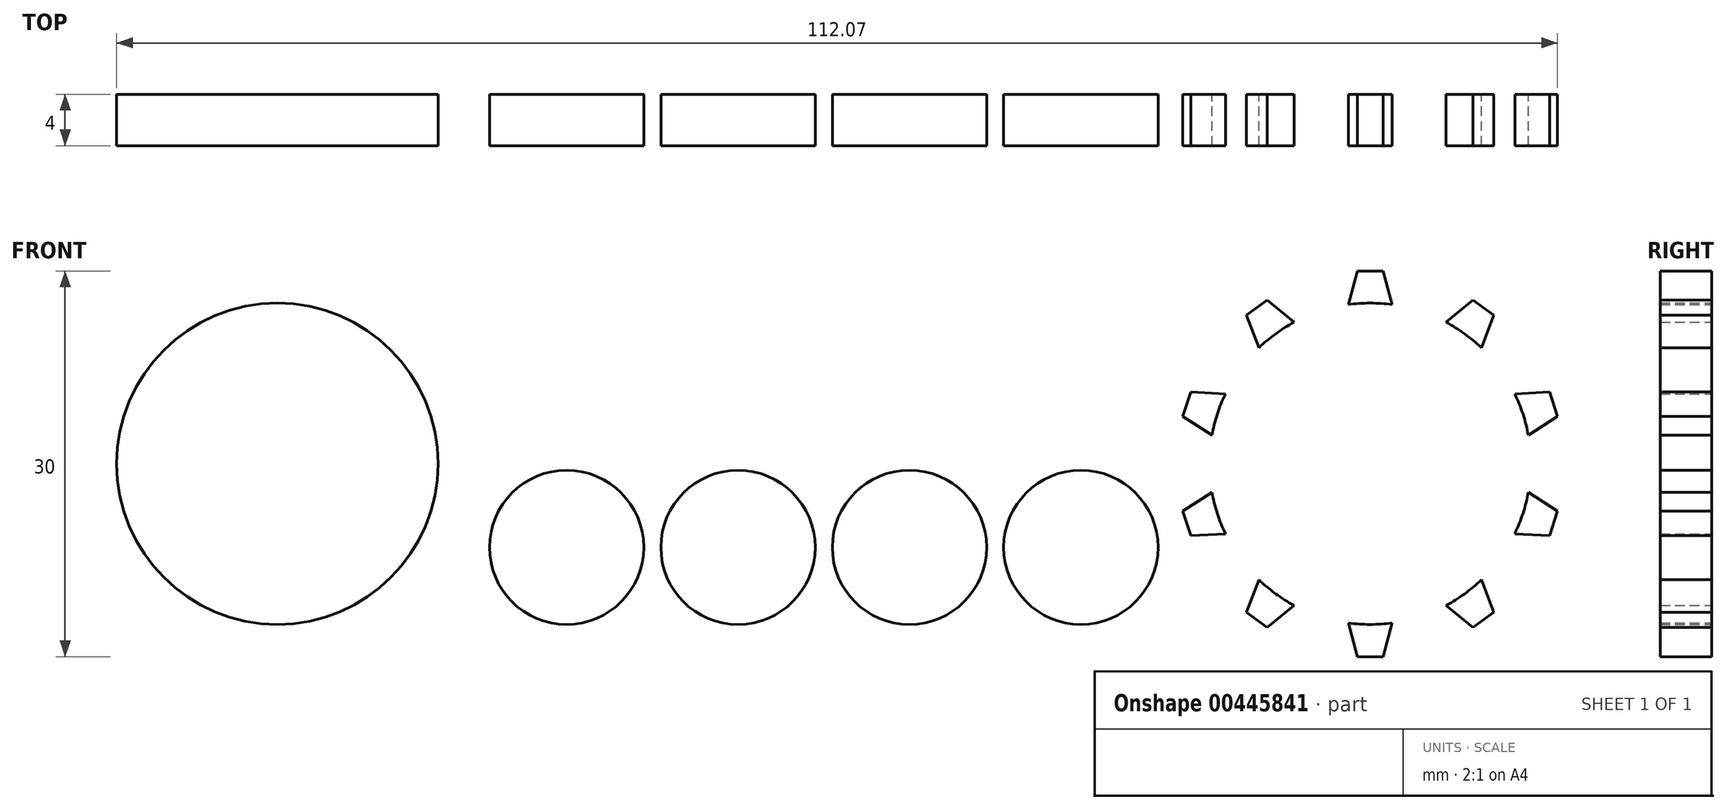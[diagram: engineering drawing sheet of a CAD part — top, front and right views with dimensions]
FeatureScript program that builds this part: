
annotation { "Feature Type Name" : "Feature", "Feature Type Description" : "" }
export const myFeature = defineFeature(function(context is Context, id is Id, definition is map)
    precondition{}
    {
        {
            var Q0;
            Q0=qCreatedBy(makeId("Front.planeOp"),FACE);
            var sketch = newSketch(context, id + "F0", { "sketchPlane" : qUnion([Q0])});
            skLineSegment(sketch, "E0.bottom", {"start": v(-42.5, 0) * mm, "end": v(42.5, 0) * mm, "construction": true});
            skCircle(sketch, "E1", {"center": v(-42.5, 12.5) * mm, "radius": 12.5 * mm});
            skCircle(sketch, "E2.MirrorC", {"center": v(42.5, 12.5) * mm, "radius": 12.5 * mm});
            skCircle(sketch, "E3", {"center": v(-20, 6) * mm, "radius": 6 * mm});
            skCircle(sketch, "E4", {"center": v(6.67, 6) * mm, "radius": 6 * mm});
            skCircle(sketch, "E5", {"center": v(20, 6) * mm, "radius": 6 * mm});
            skCircle(sketch, "E6", {"center": v(-6.67, 6) * mm, "radius": 6 * mm});
            skLineSegment(sketch, "E7", {"start": v(-20, 6) * mm, "end": v(-6.67, 6) * mm, "construction": true});
            skLineSegment(sketch, "E8", {"start": v(6.67, 6) * mm, "end": v(-6.67, 6) * mm, "construction": true});
            skLineSegment(sketch, "E9", {"start": v(20, 6) * mm, "end": v(6.67, 6) * mm, "construction": true});
            skLineSegment(sketch, "E10", {"start": v(0, 6) * mm, "end": v(0, 0) * mm, "construction": true});
            skLineSegment(sketch, "E11", {"start": v(42.5, 0) * mm, "end": v(42.5, -2.5) * mm, "construction": true});
            skLineSegment(sketch, "E12", {"start": v(42.5, -2.5) * mm, "end": v(43.5, -2.5) * mm});
            skLineSegment(sketch, "E13", {"start": v(43.5, -2.5) * mm, "end": v(44.2, 0.12) * mm});
            skLineSegment(sketch, "E14.MirrorCS", {"start": v(42.5, -2.5) * mm, "end": v(41.5, -2.5) * mm});
            skLineSegment(sketch, "E15.MirrorCS", {"start": v(41.5, -2.5) * mm, "end": v(40.8, 0.12) * mm});
            skSolve(sketch);
        }
        {
            var Q0;
            {var subQ0=sQuery(id+"F0.wireOp",EDGE,"E2.MirrorC");var subQ1=makeQuery(id+"F0.imprint","INTERSECT",VERTEX,{"derivedFrom":[subQ0,sQuery(id+"F0.wireOp",EDGE,"E13")]});Q0=makeQuery(id+"F0.imprint","IMPRINT",FACE,{"disambiguationData":[TD([[makeQuery(id+"F0.imprint","IMPRINT",EDGE,{"disambiguationData":[TD([[subQ1,-1.0]])],"derivedFrom":subQ0}),-1.0]])]});}
            var Q1;
            Q1=makeQuery(id+"F0.imprint","IMPRINT",FACE,{"disambiguationData":[TD([[makeQuery(id+"F0.imprint","IMPRINT",EDGE,{"derivedFrom":sQuery(id+"F0.wireOp",EDGE,"E12")}),1.0]])]});
            var Q2;
            Q2=makeQuery(id+"F0.imprint","IMPRINT",FACE,{"disambiguationData":[TD([[makeQuery(id+"F0.imprint","IMPRINT",EDGE,{"derivedFrom":sQuery(id+"F0.wireOp",EDGE,"E5")}),1.0]])]});
            var Q3;
            Q3=makeQuery(id+"F0.imprint","IMPRINT",FACE,{"disambiguationData":[TD([[makeQuery(id+"F0.imprint","IMPRINT",EDGE,{"derivedFrom":sQuery(id+"F0.wireOp",EDGE,"E4")}),1.0]])]});
            var Q4;
            Q4=makeQuery(id+"F0.imprint","IMPRINT",FACE,{"disambiguationData":[TD([[makeQuery(id+"F0.imprint","IMPRINT",EDGE,{"derivedFrom":sQuery(id+"F0.wireOp",EDGE,"E6")}),1.0]])]});
            var Q5;
            Q5=makeQuery(id+"F0.imprint","IMPRINT",FACE,{"disambiguationData":[TD([[makeQuery(id+"F0.imprint","IMPRINT",EDGE,{"derivedFrom":sQuery(id+"F0.wireOp",EDGE,"E3")}),1.0]])]});
            var Q6;
            Q6=makeQuery(id+"F0.imprint","IMPRINT",FACE,{"disambiguationData":[TD([[makeQuery(id+"F0.imprint","IMPRINT",EDGE,{"derivedFrom":sQuery(id+"F0.wireOp",EDGE,"E1")}),1.0]])]});
            extrude(context, id + "F1", {"entities" : qUnion([Q0, Q1, Q2, Q3, Q4, Q5, Q6]), "endBound" : BoundingType.SYMMETRIC, "depth" : 4 * mm});
        }
        {
            var Q0;
            Q0=makeQuery(id+"F1.opExtrude","SWEPT_BODY",BODY,{"disambiguationData":[OSD([sQuery(id+"F0.wireOp",EDGE,"E2.MirrorC"),sQuery(id+"F0.wireOp",EDGE,"E12"),sQuery(id+"F0.wireOp",EDGE,"E13"),sQuery(id+"F0.wireOp",EDGE,"E14.MirrorCS"),sQuery(id+"F0.wireOp",EDGE,"E15.MirrorCS")])]});
            var Q1;
            Q1=sQuery(id+"F0.wireOp",EDGE,"E2.MirrorC");
            circularPattern(context, id + "F2", {"operationType" : NewBodyOperationType.ADD, "entities" : qUnion([Q0]), "axis" : qUnion([Q1]), "angle" : 360 * degree, "instanceCount" : 10, "equalSpace" : true});
        }
    });
